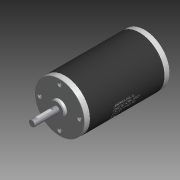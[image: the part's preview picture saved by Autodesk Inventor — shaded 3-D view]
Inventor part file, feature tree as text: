
AUTODESK INVENTOR PART (.ipt)
format: ipt  version: 2014 (Build 180170000, 170)  size: 6,454,272 bytes
history: native  units: mm (DEFAULTED — no unit token found)
features: sketch x10, extrude x7, chamfer x4, hole x2, pattern_circular x2, fillet x2, plane x2, emboss x1
ambient origin geometry x8: Origin, YZ Plane, XZ Plane, XY Plane, X Axis, Y Axis, Z Axis, Center Point
bodies: Solid1 (feature_tree)
feature tree (30):
  extrude  "Extrusion1"  Depth=7.0mm TaperAngle=0.0deg
  extrude  "Extrusion2"  Depth=3.9878mm TaperAngle=0.0deg
  chamfer  "Chamfer1"  Distance=1.0mm
  hole  "Hole2"  [1 undecoded]
  pattern_circular  "Circular Pattern2"  Count=4 Angle=90.0deg
  chamfer  "Chamfer3"  Distance=31.623mm
  extrude  "Extrusion3"  Depth=12.7mm
  fillet  "Fillet1"  Radius=64.4144mm
  extrude  "Extrusion5"  Depth=64.008mm
  extrude  "Extrusion6"  Depth=30.1498mm
  extrude  "Extrusion7"  Depth=0.508mm
  hole  "Hole3"  [1 undecoded]
  chamfer  "Chamfer2"  Distance=20.0mm Angle=360.0deg
  pattern_circular  "Circular Pattern3"  [2 undecoded]
  fillet  "Fillet2"  [1 undecoded]
  chamfer  "Chamfer4"  Distance=1.99898mm
  plane  "Work Plane1"
  extrude  "Extrusion8"  Depth=20.09902mm
  plane  "Work Plane2"
  emboss  "Emboss1"
  sketch  "Sketch1"  dims[d0=64.008mm d1=7.0mm d2=0.0mm]
  sketch  "Sketch2"  dims[d3=19.05mm d4=3.9878mm d5=0.0mm d6=1.0mm d7=1.0mm]
  sketch  "Sketch4"  dims[d18=3.9624mm d19=9.525mm d20=6.35mm d21=60.0deg d22=19.05mm d23=20.594885mm d24=25.4mm d25=40.0mm d27=90.0deg]
  sketch  "Sketch5"  dims[d28=7.9502mm d29=31.623mm d30=0.0mm]
  sketch  "Sketch8"  dims[d31=0.79375mm d33=12.7mm d38=64.4144mm]
  sketch  "Sketch9"  dims[d39=95.6056mm d40=0.0mm d41=64.008mm]
  sketch  "Sketch10"  dims[d42=7.0mm d43=0.0mm d44=30.1498mm]
  sketch  "Sketch11"  dims[d45=4.1148mm d46=0.0mm]
  sketch  "Sketch12"  dims[d47=5.08mm d48=12.7mm d49=9.906mm d50=4.572mm d51=14.3117mm d52=7.62mm d53=20.594885mm d54=0.508mm d55=3.175mm]
  sketch  "Sketch13"  dims[d56=0.762mm d57=0.762mm d58=3.175mm d59=20.0mm d61=360.0deg d62=0.25mm d63=3.175mm d64=45.0deg d65=45.0deg d66=45.0deg d67=45.0deg d68=1.99898mm d70=20.09902mm d71=7.99338mm d72=1.15062mm d73=0.0mm d74=30.48mm d75=0.0254mm d76=0.0mm]
note: 5 required parameter values undecoded (feature->parameter linkage not recoverable at this tier; creation-order binding heuristic only, values carry confidence <= 0.55)
